# Revit family: Lavatory-Pedestal_Traditional_LPT790_TOTO
name_source: partatom
category: Plumbing Fixtures
revit_build: Autodesk Revit Architecture 2013 (Build: 20130531_2115(x64)
units: mm (PartAtom-declared; Revit-internal decimal feet)

## types (1)
- LPT790
    04 CSI = 22 42 16
    95 CSI = 15410
    ADA Compliant = No
    Assembly Code = D2010310
    Basin Depth = 11"
    Basin Width = 15 3/4"
    CAD Drawing URL = http://assets.totousa.com
    CW Connection = Yes
    CWFU = 0
    Certifications = IAPMO(cUPC), State of Massachusetts , City of Los Angeles, and others
    Code Compliance = UPC, IPC, NSPC, NPC Canada, and others
    Cold Water Connection Diameter = 0"
    Cold Water Connection Radius = 3/16"
    Cold Water Connector = Cold Water Connection
    Color Availability = #01 Cotton, #03 Bone, #11 Colonial White, #12 Sedona Beige, #51 Ebony
    Default Elevation = 0"
    Depth = 17 29/32"
    Description = Pedestal Lavatory with Single Hole
    Finish = Vitreous China - TOTO - 01 Cotton
    HW Connection = Yes
    HWFU = 0
    Height = 34 1/4"
    Hot Water Connection Diameter = 0"
    Hot Water Connection Radius = 3/16"
    Hot Water Connector = Hot Water Connection
    Industry Standards = Meets and exceeds ASME A112.19.2/CSA B45.1
    Manufacturer = TOTO USA, Inc.
    Manufacturer Fax = (770) 282-0002
    Material = Vitreous China
    Model = LPT790
    Mounting = Pedestal
    Sanitary Connector = Sanitary Connection
    SanoGloss Available = No
    Series = Nexus
    Shipping Weight = 71.50 lb
    Sink Configuration = Single Sink
    Sink Type = Lavatory
    Spec Sheet URL = http://assets.totousa.com
    Style = Traditional
    Subcategory = Lavatories
    Toto BIM Number = BM-00196
    URL = http://www.totousa.com
    Vent Connection = Yes
    WFU = 0
    Warranty = One Year Limited Warranty
    Warranty URL = http://www.totousa.com
    Waste Connection = Yes
    Waste Connection NPT Radius = 5/8"
    Width = 24 1/32"

## geometry (parser evidence)
native form markers: Blend x2, Sweep x4
no freeform markers — native parametric forms only
